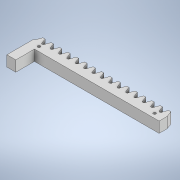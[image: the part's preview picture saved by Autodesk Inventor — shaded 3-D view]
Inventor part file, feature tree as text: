
AUTODESK INVENTOR PART (.ipt)
format: ipt  version: 2021 (Build 250183000, 183)  size: 207,872 bytes
history: native  units: in
note: dims shown in document units (in); Inventor stores cm internally (conversion verified against a paired STEP export)
features: extrude x2, sketch x2
ambient origin geometry x8: Origin, YZ Plane, XZ Plane, XY Plane, X Axis, Y Axis, Z Axis, Center Point
bodies: Solid1 (feature_tree), Solid2 (feature_tree)
feature tree (4):
  extrude  "Extrusion4"  Depth=1.1811in
  extrude  "Extrusion6"  Depth=0.3937in
  sketch  "Sketch4"  dims[d14=0.4724in d15=1.1811in]
  sketch  "Sketch6"  dims[d16=0.3937in d17=0.0in d23=0.1181in d24=0.1181in d25=0.1969in d26=0.1969in d27=0.3937in d28=0.3937in d29=0.0in d30=0.0in d3=0.0197in d4=1.9685in d5=0.0197in d6=1.9685in]
